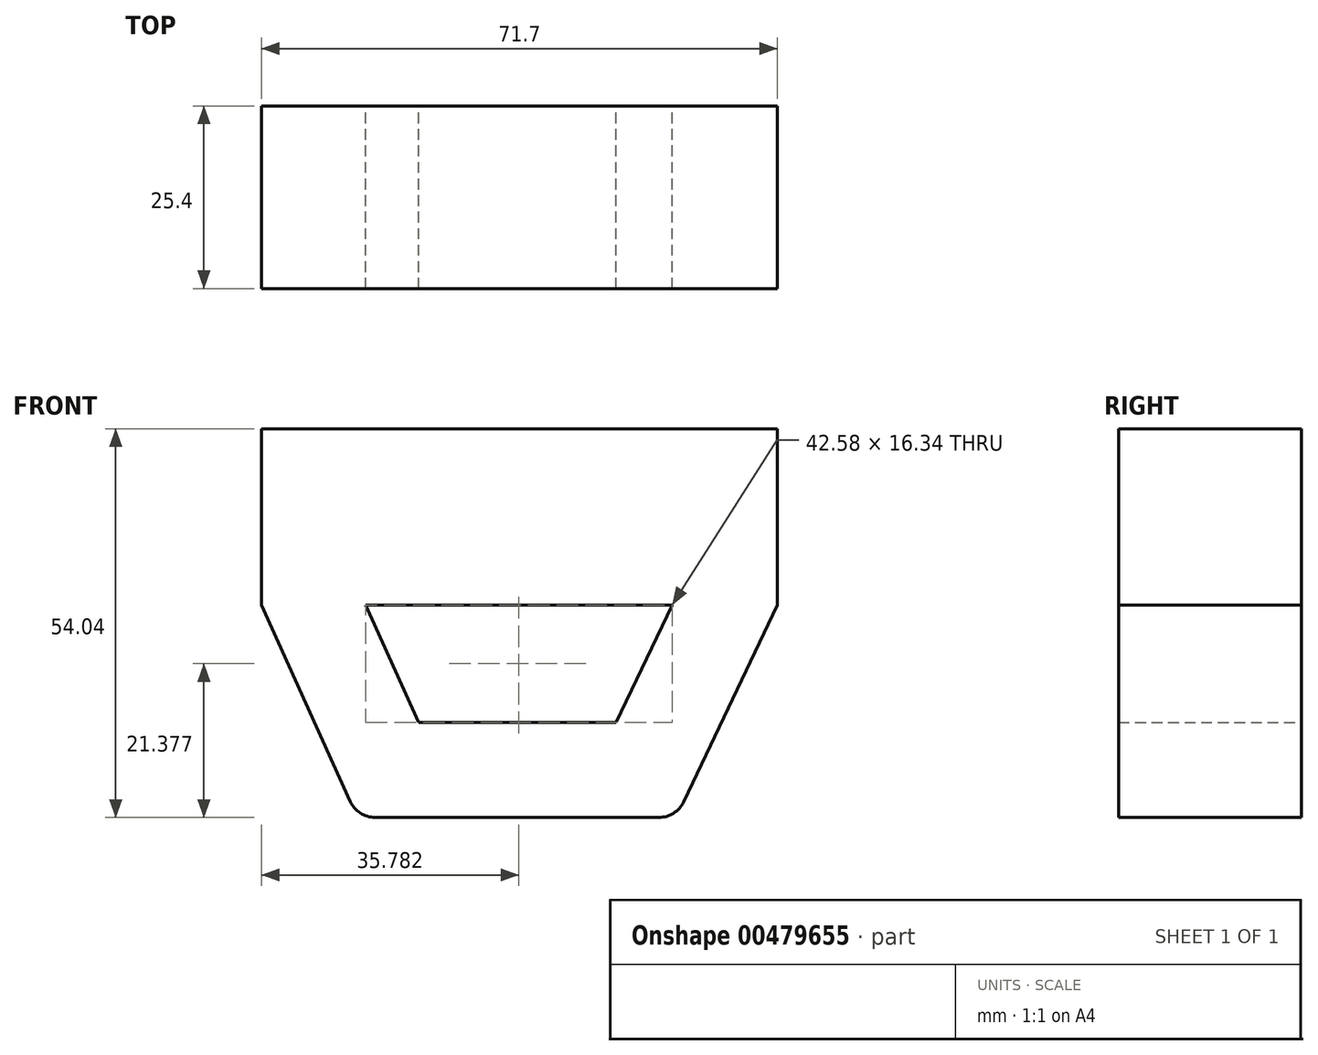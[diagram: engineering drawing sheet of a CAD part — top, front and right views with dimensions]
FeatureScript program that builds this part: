
annotation { "Feature Type Name" : "Feature", "Feature Type Description" : "" }
export const myFeature = defineFeature(function(context is Context, id is Id, definition is map)
    precondition{}
    {
        {
            var Q0;
            Q0=qCreatedBy(makeId("Front.planeOp"),FACE);
            var sketch = newSketch(context, id + "F0", { "sketchPlane" : qUnion([Q0])});
            skLineSegment(sketch, "E0.bottom", {"start": v(-36.03, 43.6) * mm, "end": v(35.67, 43.6) * mm});
            skLineSegment(sketch, "E0.top", {"start": v(-36.03, 19.1) * mm, "end": v(35.67, 19.1) * mm});
            skLineSegment(sketch, "E0.left", {"start": v(-36.03, 43.6) * mm, "end": v(-36.03, 19.1) * mm});
            skLineSegment(sketch, "E0.right", {"start": v(35.67, 43.6) * mm, "end": v(35.67, 19.1) * mm});
            skLineSegment(sketch, "E1", {"start": v(-36.03, 19.1) * mm, "end": v(-23.71, -8.2) * mm});
            skLineSegment(sketch, "E2", {"start": v(-20.24, -10.45) * mm, "end": v(19.21, -10.45) * mm});
            skLineSegment(sketch, "E3", {"start": v(22.65, -8.27) * mm, "end": v(35.67, 19.1) * mm});
            skLineSegment(sketch, "E4", {"start": v(0, -10.45) * mm, "end": v(0, 19.1) * mm, "construction": true});
            skPoint(sketch, "E5.visualSharp", {"position": v(-22.7, -10.45) * mm});
            skArc(sketch, "E5.filletArc", {"start": v(-23.71, -8.2) * mm, "mid": v(-22.3, -9.84) * mm, "end": v(-20.24, -10.45) * mm});
            skPoint(sketch, "E6.visualSharp", {"position": v(21.62, -10.45) * mm});
            skArc(sketch, "E6.filletArc", {"start": v(19.21, -10.45) * mm, "mid": v(21.25, -9.86) * mm, "end": v(22.65, -8.27) * mm});
            skLineSegment(sketch, "E7.0", {"start": v(13.27, 2.76) * mm, "end": v(21.04, 19.1) * mm});
            skLineSegment(sketch, "E7.1", {"start": v(-14.17, 2.76) * mm, "end": v(13.27, 2.76) * mm});
            skLineSegment(sketch, "E7.2", {"start": v(-21.54, 19.1) * mm, "end": v(-14.17, 2.76) * mm});
            skSolve(sketch);
        }
        {
            var Q0;
            Q0 = qSketchRegion(id + "F0", true);
            extrude(context, id + "F1", {"entities" : qUnion([Q0]), "depth" : 25.4 * mm});
        }
    });
